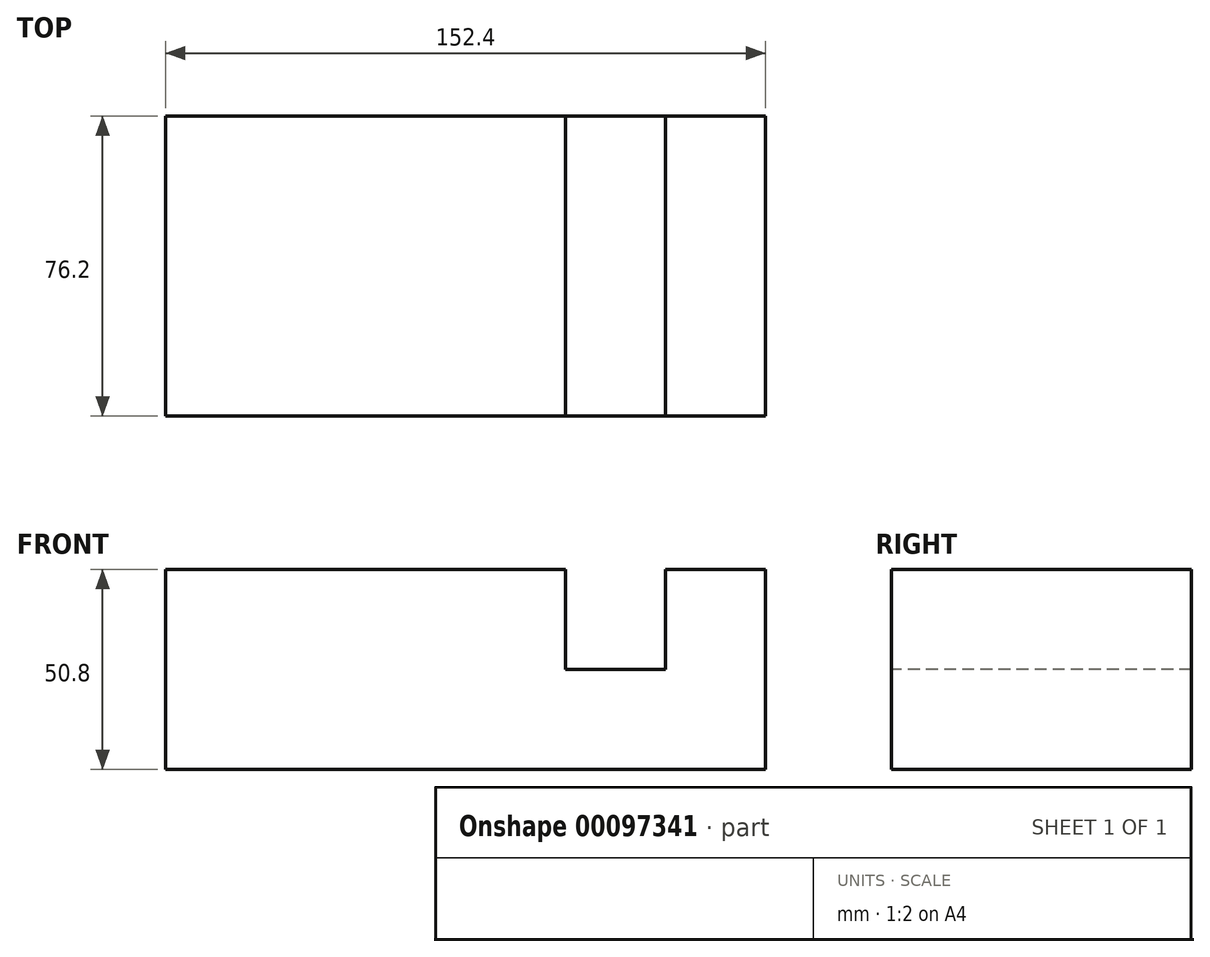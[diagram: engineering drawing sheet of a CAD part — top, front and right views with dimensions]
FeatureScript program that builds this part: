
annotation { "Feature Type Name" : "Feature", "Feature Type Description" : "" }
export const myFeature = defineFeature(function(context is Context, id is Id, definition is map)
    precondition{}
    {
        {
            var Q0;
            Q0=qCreatedBy(makeId("Front.planeOp"),FACE);
            var sketch = newSketch(context, id + "F0", { "sketchPlane" : qUnion([Q0])});
            skLineSegment(sketch, "E0.bottom", {"start": v(-76.2, 0) * mm, "end": v(76.2, 0) * mm});
            skLineSegment(sketch, "E0.top", {"start": v(-76.2, 50.8) * mm, "end": v(76.2, 50.8) * mm});
            skLineSegment(sketch, "E0.left", {"start": v(-76.2, 0) * mm, "end": v(-76.2, 50.8) * mm});
            skLineSegment(sketch, "E0.right", {"start": v(76.2, 0) * mm, "end": v(76.2, 50.8) * mm});
            skSolve(sketch);
        }
        {
            var Q0;
            Q0=makeQuery(id+"F0.imprint","IMPRINT",FACE,{"disambiguationData":[TD([[makeQuery(id+"F0.imprint","IMPRINT",EDGE,{"derivedFrom":sQuery(id+"F0.wireOp",EDGE,"E0.bottom")}),1.0]])]});
            extrude(context, id + "F1", {"entities" : qUnion([Q0]), "depth" : 76.2 * mm, "symmetric" : true});
        }
        {
            var Q0;
            Q0=makeQuery(id+"F1.opExtrude","CAP_FACE",FACE,{"disambiguationData":[OSD([sQuery(id+"F0.wireOp",EDGE,"E0.bottom"),sQuery(id+"F0.wireOp",EDGE,"E0.top"),sQuery(id+"F0.wireOp",EDGE,"E0.left"),sQuery(id+"F0.wireOp",EDGE,"E0.right")])],"isStart":false});
            var sketch = newSketch(context, id + "F2", { "sketchPlane" : qUnion([Q0])});
            skLineSegment(sketch, "E1.bottom", {"start": v(25.4, 50.8) * mm, "end": v(50.8, 50.8) * mm});
            skLineSegment(sketch, "E1.top", {"start": v(25.4, 25.4) * mm, "end": v(50.8, 25.4) * mm});
            skLineSegment(sketch, "E1.left", {"start": v(25.4, 50.8) * mm, "end": v(25.4, 25.4) * mm});
            skLineSegment(sketch, "E1.right", {"start": v(50.8, 50.8) * mm, "end": v(50.8, 25.4) * mm});
            skSolve(sketch);
        }
        {
            var Q0;
            Q0=makeQuery(id+"F2.imprint","IMPRINT",FACE,{"disambiguationData":[TD([[makeQuery(id+"F2.imprint","IMPRINT",EDGE,{"derivedFrom":sQuery(id+"F2.wireOp",EDGE,"E1.bottom")}),-1.0]])]});
            extrude(context, id + "F3", {"entities" : qUnion([Q0]), "operationType" : NewBodyOperationType.REMOVE, "endBound" : BoundingType.THROUGH_ALL, "oppositeDirection" : true, "depth" : 25.4 * mm});
        }
    });
